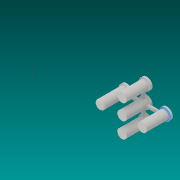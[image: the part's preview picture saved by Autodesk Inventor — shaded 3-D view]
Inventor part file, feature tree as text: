
AUTODESK INVENTOR PART (.ipt)
format: ipt  version: 2019 (Build 230136000, 136)  size: 207,360 bytes
history: native  units: mm
features: boolean_combine x6, other x5, sketch x3, extrude x1, fillet x1
ambient origin geometry x8: Origin, YZ Plane, XZ Plane, XY Plane, X Axis, Y Axis, Z Axis, Center Point
bodies: Solid1 (feature_tree), Solid2 (feature_tree), Solid6 (feature_tree), Solid7 (feature_tree), Solid8 (feature_tree), Solid9 (feature_tree), Solid10 (feature_tree), Solid3 (feature_tree), Solid4 (feature_tree), Solid5 (feature_tree)
feature tree (16):
  other  "Repaired Geometry1"
  sketch  "Sketch3"  dims[d0=1.0mm d1=0.0mm d2=0.5mm]
  boolean_combine  "Combine1"
  boolean_combine  "Combine2"
  boolean_combine  "Combine3"
  boolean_combine  "Combine4"
  boolean_combine  "Combine5"
  boolean_combine  "Combine6"
  extrude  "Extrusion1"  Depth=0.5mm
  fillet  "Fillet1"  [1 undecoded]
  sketch  "Sketch8"
  sketch  "Sketch4"
  other  "Solid6:1"
  other  "Solid6:2"
  other  "Solid6:3"
  other  "Solid5:1"
note: 1 required parameter value undecoded (feature->parameter linkage not recoverable at this tier; creation-order binding heuristic only, values carry confidence <= 0.55)
